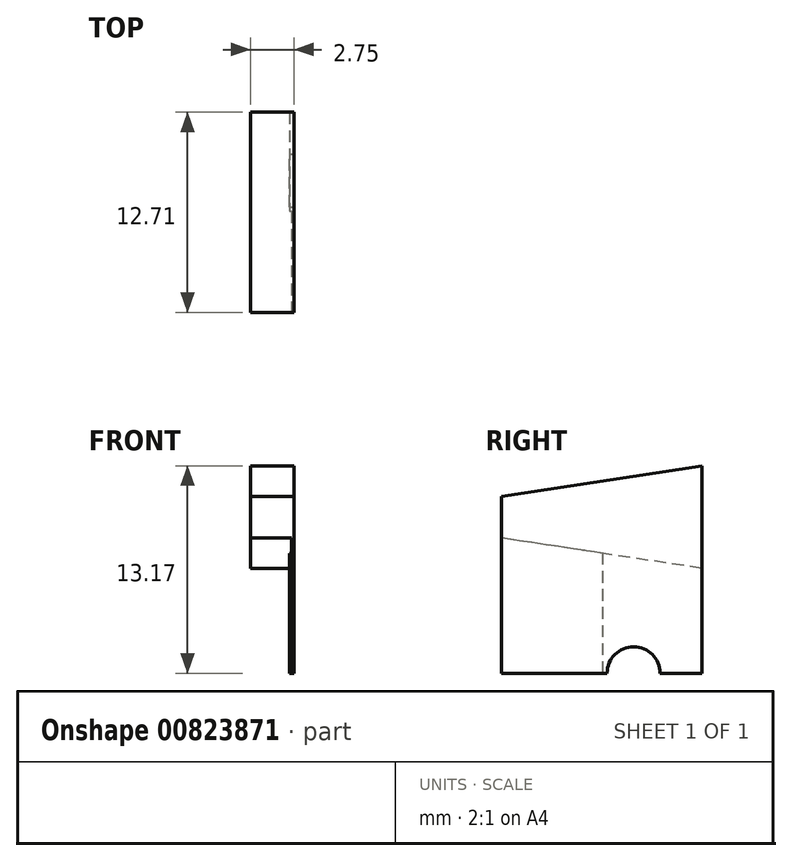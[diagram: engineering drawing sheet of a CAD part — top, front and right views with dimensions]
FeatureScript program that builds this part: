
annotation { "Feature Type Name" : "Feature", "Feature Type Description" : "" }
export const myFeature = defineFeature(function(context is Context, id is Id, definition is map)
    precondition{}
    {
        {
            assignVariable(context, id + "F0", {"name" : "C", "anyValue" : .5186});
        }
        {
            assignVariable(context, id + "F1", {"name" : "F", "anyValue" : 0.29});
        }
        {
            assignVariable(context, id + "F2", {"name" : "G", "anyValue" : .1567});
        }
        {
            assignVariable(context, id + "F3", {"name" : "I", "anyValue" : 2.75});
        }
        {
            var Q0;
            Q0=qCreatedBy(makeId("Right.planeOp"),FACE);
            var sketch = newSketch(context, id + "F4", { "sketchPlane" : qUnion([Q0])});
            skLineSegment(sketch, "E0", {"start": v(0, 11.24) * mm, "end": v(12.71, 13.17) * mm});
            skLineSegment(sketch, "E1", {"start": v(12.71, 13.17) * mm, "end": v(12.71, 6.66) * mm});
            skLineSegment(sketch, "E2", {"start": v(12.71, 6.66) * mm, "end": v(0, 8.6) * mm});
            skLineSegment(sketch, "E3", {"start": v(0, 11.24) * mm, "end": v(0, 8.6) * mm});
            skLineSegment(sketch, "E4", {"start": v(12.71, 9.92) * mm, "end": v(0, 9.92) * mm, "construction": true});
            skSolve(sketch);
        }
        {
            var Q0;
            Q0=makeQuery(id+"F4.imprint","IMPRINT",FACE,{"disambiguationData":[TD([[makeQuery(id+"F4.imprint","IMPRINT",EDGE,{"derivedFrom":sQuery(id+"F4.wireOp",EDGE,"E0")}),-1.0]])]});
            extrude(context, id + "F5", {"entities" : qUnion([Q0]), "oppositeDirection" : true, "depth" : (getVariable(context, 'I')) * mm, "offsetDistance" : 25.4 * mm});
        }
        {
            var Q0;
            Q0=makeQuery(id+"F5.opExtrude","CAP_FACE",FACE,{"disambiguationData":[OSD([sQuery(id+"F4.wireOp",EDGE,"E0"),sQuery(id+"F4.wireOp",EDGE,"E1"),sQuery(id+"F4.wireOp",EDGE,"E2"),sQuery(id+"F4.wireOp",EDGE,"E3")])],"isStart":true});
            var sketch = newSketch(context, id + "F6", { "sketchPlane" : qUnion([Q0])});
            skLineSegment(sketch, "E5", {"start": v(12.71, 6.66) * mm, "end": v(12.71, 0) * mm});
            skLineSegment(sketch, "E6", {"start": v(12.71, 0) * mm, "end": v(0, 0) * mm});
            skLineSegment(sketch, "E7", {"start": v(0, 0) * mm, "end": v(0, 8.6) * mm});
            skLineSegment(sketch, "E8", {"start": v(0, 8.6) * mm, "end": v(12.71, 6.66) * mm});
            skSolve(sketch);
        }
        {
            var Q0;
            Q0=makeQuery(id+"F6.imprint","IMPRINT",FACE,{"disambiguationData":[TD([[makeQuery(id+"F6.imprint","IMPRINT",EDGE,{"derivedFrom":sQuery(id+"F6.wireOp",EDGE,"E5")}),-1.0]])]});
            extrude(context, id + "F7", {"entities" : qUnion([Q0]), "operationType" : NewBodyOperationType.ADD, "oppositeDirection" : true, "depth" : (getVariable(context, 'G')) * mm, "offsetDistance" : 25.4 * mm});
        }
        {
            var Q0;
            Q0=makeQuery(id+"F7.opExtrude","CAP_FACE",FACE,{"disambiguationData":[OSD([sQuery(id+"F6.wireOp",EDGE,"E5"),sQuery(id+"F6.wireOp",EDGE,"E6"),sQuery(id+"F6.wireOp",EDGE,"E7"),sQuery(id+"F6.wireOp",EDGE,"E8")])],"isStart":false});
            var sketch = newSketch(context, id + "F8", { "sketchPlane" : qUnion([Q0])});
            skLineSegment(sketch, "E9", {"start": v(-12.71, 6.66) * mm, "end": v(-12.71, 0) * mm});
            skLineSegment(sketch, "E10", {"start": v(-12.71, 0) * mm, "end": v(-6.44, 0) * mm});
            skLineSegment(sketch, "E11", {"start": v(-6.44, 0) * mm, "end": v(-6.44, 7.61) * mm});
            skLineSegment(sketch, "E12", {"start": v(-6.44, 7.61) * mm, "end": v(-12.71, 6.66) * mm});
            skSolve(sketch);
        }
        {
            var Q0;
            Q0=makeQuery(id+"F8.imprint","IMPRINT",FACE,{"disambiguationData":[TD([[makeQuery(id+"F8.imprint","IMPRINT",EDGE,{"derivedFrom":sQuery(id+"F8.wireOp",EDGE,"E9")}),1.0]])]});
            extrude(context, id + "F9", {"entities" : qUnion([Q0]), "operationType" : NewBodyOperationType.ADD, "depth" : (getVariable(context, 'F') - getVariable(context, 'G')) * mm, "offsetDistance" : 25.4 * mm});
        }
        {
            var Q0;
            Q0=makeQuery(id+"F9.boolean.opBoolean","MERGE",FACE,{"derivedFrom":[makeQuery(id+"F7.opExtrude","SWEPT_FACE",FACE,{"disambiguationData":[OSD([sQuery(id+"F6.wireOp",EDGE,"E6")])]}),makeQuery(id+"F9.opExtrude","SWEPT_FACE",FACE,{"disambiguationData":[OSD([sQuery(id+"F8.wireOp",EDGE,"E10")])]})]});
            var sketch = newSketch(context, id + "F10", { "sketchPlane" : qUnion([Q0])});
            skLineSegment(sketch, "E13.bottom", {"start": v(-3.98, -6.44) * mm, "end": v(-8.3, -6.44) * mm});
            skLineSegment(sketch, "E13.top", {"start": v(-3.98, 0) * mm, "end": v(-8.3, 0) * mm});
            skLineSegment(sketch, "E13.left", {"start": v(-3.98, -6.44) * mm, "end": v(-3.98, 0) * mm});
            skLineSegment(sketch, "E13.right", {"start": v(-8.3, -6.44) * mm, "end": v(-8.3, 0) * mm});
            skSolve(sketch);
        }
        {
            var Q0;
            Q0 = qSketchRegion(id + "F10", true);
            extrude(context, id + "F11", {"entities" : qUnion([Q0]), "operationType" : NewBodyOperationType.REMOVE, "oppositeDirection" : true, "depth" : 25.4 * mm, "offsetDistance" : 25.4 * mm});
        }
        {
            var Q0;
            Q0=makeQuery(id+"F7.boolean.opBoolean","MERGE",FACE,{"derivedFrom":[makeQuery(id+"F5.opExtrude","CAP_FACE",FACE,{"disambiguationData":[OSD([sQuery(id+"F4.wireOp",EDGE,"E0"),sQuery(id+"F4.wireOp",EDGE,"E1"),sQuery(id+"F4.wireOp",EDGE,"E2"),sQuery(id+"F4.wireOp",EDGE,"E3")])],"isStart":true}),makeQuery(id+"F7.opExtrude","CAP_FACE",FACE,{"disambiguationData":[OSD([sQuery(id+"F6.wireOp",EDGE,"E5"),sQuery(id+"F6.wireOp",EDGE,"E6"),sQuery(id+"F6.wireOp",EDGE,"E7"),sQuery(id+"F6.wireOp",EDGE,"E8")])],"isStart":true})]});
            var sketch = newSketch(context, id + "F12", { "sketchPlane" : qUnion([Q0])});
            skCircle(sketch, "E14", {"center": v(8.39, 0) * mm, "radius": 1.68 * mm});
            skSolve(sketch);
        }
        {
            var Q0;
            Q0 = qSketchRegion(id + "F12", true);
            extrude(context, id + "F13", {"entities" : qUnion([Q0]), "operationType" : NewBodyOperationType.REMOVE, "endBound" : BoundingType.THROUGH_ALL, "oppositeDirection" : true, "depth" : 25.4 * mm, "offsetDistance" : 25.4 * mm});
        }
        {
            var Q0;
            Q0=qCreatedBy(makeId("Top.planeOp"),FACE);
            cPlane(context, id + "F14", {"entities" : qUnion([Q0]), "cplaneType" : CPlaneType.OFFSET, "offset" : (getVariable(context, 'C')) * mm, "width" : 152.4 * mm, "height" : 152.4 * mm});
        }
        {
            var Q0;
            Q0=qCreatedBy(id+"F14.planeOp",FACE);
            var sketch = newSketch(context, id + "F15", { "sketchPlane" : qUnion([Q0])});
            skLineSegment(sketch, "E15", {"start": v(-69.91, 0) * mm, "end": v(-69.91, 12.71) * mm});
            skLineSegment(sketch, "E16", {"start": v(-69.91, 12.71) * mm, "end": v(-69.06, 12.71) * mm});
            skLineSegment(sketch, "E17", {"start": v(-69.06, 12.71) * mm, "end": v(-69.91, 0) * mm});
            skSolve(sketch);
        }
        {
            var Q0;
            Q0 = qSketchRegion(id + "F15", true);
            extrude(context, id + "F16", {"entities" : qUnion([Q0]), "operationType" : NewBodyOperationType.REMOVE, "endBound" : BoundingType.THROUGH_ALL, "oppositeDirection" : true, "depth" : 25.4 * mm, "offsetDistance" : 25.4 * mm});
        }
        {
            var Q0;
            Q0=qCreatedBy(id+"F14.planeOp",FACE);
            var sketch = newSketch(context, id + "F17", { "sketchPlane" : qUnion([Q0])});
            skLineSegment(sketch, "E18", {"start": v(-69.47, 6.57) * mm, "end": v(-69.2, 6.1) * mm});
            skLineSegment(sketch, "E19", {"start": v(-69.2, 6.1) * mm, "end": v(-69.52, 5.91) * mm});
            skLineSegment(sketch, "E20", {"start": v(-69.47, 6.57) * mm, "end": v(-69.52, 5.91) * mm});
            skSolve(sketch);
        }
        {
            var Q0;
            Q0 = qSketchRegion(id + "F17", true);
            extrude(context, id + "F18", {"entities" : qUnion([Q0]), "operationType" : NewBodyOperationType.REMOVE, "endBound" : BoundingType.THROUGH_ALL, "oppositeDirection" : true, "depth" : 25.4 * mm, "offsetDistance" : 25.4 * mm});
        }
    });
